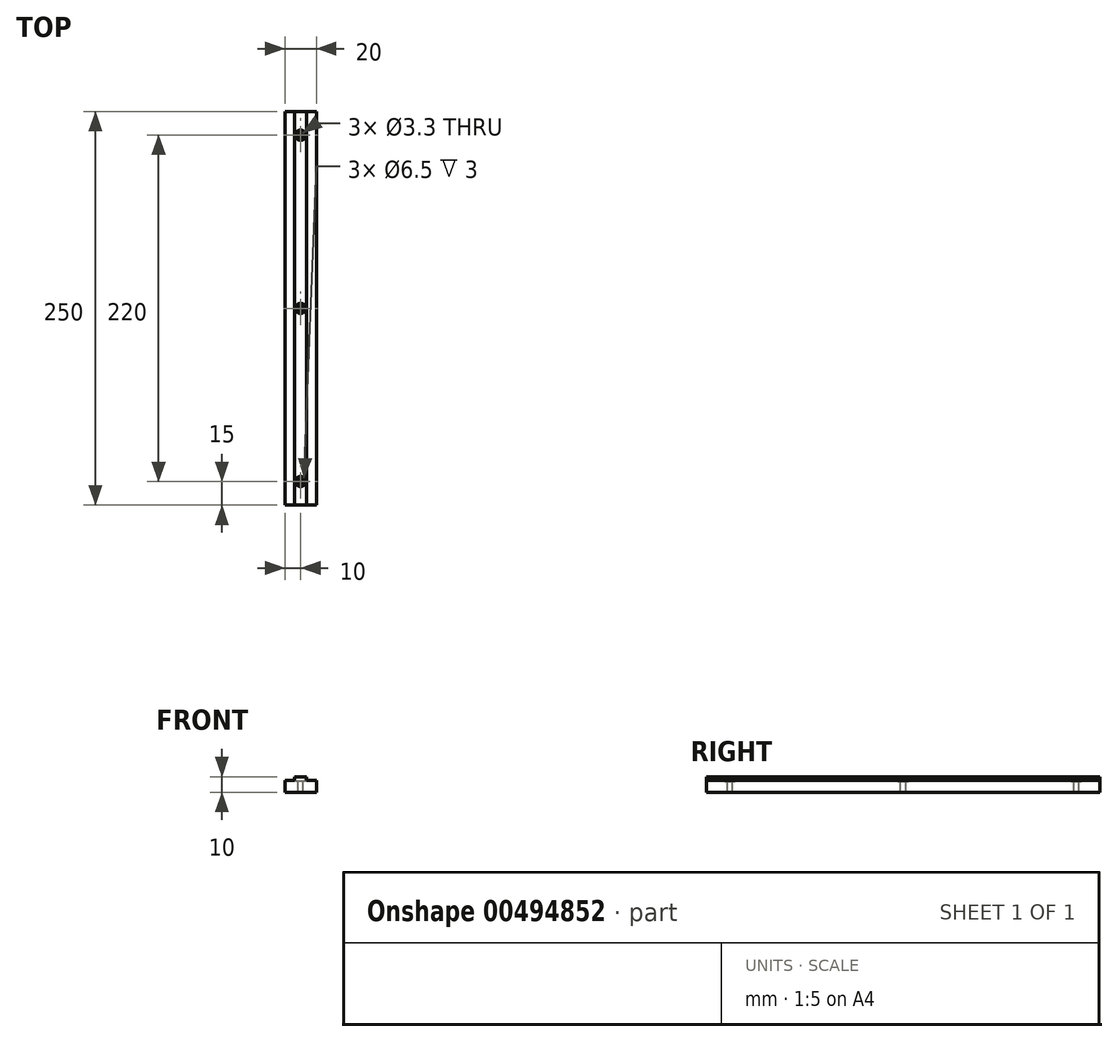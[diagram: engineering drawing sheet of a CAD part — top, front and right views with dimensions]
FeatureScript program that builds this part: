
annotation { "Feature Type Name" : "Feature", "Feature Type Description" : "" }
export const myFeature = defineFeature(function(context is Context, id is Id, definition is map)
    precondition{}
    {
        {
            var Q0;
            Q0=qCreatedBy(makeId("Front.planeOp"),FACE);
            var sketch = newSketch(context, id + "F0", { "sketchPlane" : qUnion([Q0])});
            skLineSegment(sketch, "E0.bottom", {"start": v(-10, 0) * mm, "end": v(10, 0) * mm});
            skLineSegment(sketch, "E0.top", {"start": v(-10, 7.7) * mm, "end": v(-3.8, 7.7) * mm});
            skLineSegment(sketch, "E0.left", {"start": v(-10, 0) * mm, "end": v(-10, 7.7) * mm});
            skLineSegment(sketch, "E0.right", {"start": v(10, 0) * mm, "end": v(10, 7.7) * mm});
            skLineSegment(sketch, "E1.top", {"start": v(-3.8, 10) * mm, "end": v(3.8, 10) * mm});
            skLineSegment(sketch, "E1.left", {"start": v(-3.8, 7.7) * mm, "end": v(-3.8, 10) * mm});
            skLineSegment(sketch, "E1.right", {"start": v(3.8, 7.7) * mm, "end": v(3.8, 10) * mm});
            skLineSegment(sketch, "E2.trimOffspring", {"start": v(3.8, 7.7) * mm, "end": v(10, 7.7) * mm});
            skSolve(sketch);
        }
        {
            var Q0;
            Q0=qSketchRegion(id+"F0",true);
            extrude(context, id + "F1", {"entities" : qUnion([Q0]), "oppositeDirection" : true, "depth" : 250 * mm});
        }
        {
            var Q0;
            Q0=makeQuery(id+"F1.opExtrude","SWEPT_FACE",FACE,{"disambiguationData":[OSD([sQuery(id+"F0.wireOp",EDGE,"E1.top")])]});
            var sketch = newSketch(context, id + "F2", { "sketchPlane" : qUnion([Q0])});
            skPoint(sketch, "E3", {"position": v(0, 15) * mm});
            skPoint(sketch, "E4", {"position": v(0, 125) * mm});
            skPoint(sketch, "E5", {"position": v(0, 235) * mm});
            skSolve(sketch);
        }
        {
            var Q0;
            Q0=sQuery(id+"F2.wireOp",VERTEX,"E3");
            var Q1;
            Q1=sQuery(id+"F2.wireOp",VERTEX,"E4");
            var Q2;
            Q2=sQuery(id+"F2.wireOp",VERTEX,"E5");
            var Q3;
            Q3=makeQuery(id+"F1.opExtrude","SWEPT_BODY",BODY,{"disambiguationData":[OSD([sQuery(id+"F0.wireOp",EDGE,"E0.bottom"),sQuery(id+"F0.wireOp",EDGE,"E0.top"),sQuery(id+"F0.wireOp",EDGE,"E0.left"),sQuery(id+"F0.wireOp",EDGE,"E0.right"),sQuery(id+"F0.wireOp",EDGE,"E1.top"),sQuery(id+"F0.wireOp",EDGE,"E1.left"),sQuery(id+"F0.wireOp",EDGE,"E1.right"),sQuery(id+"F0.wireOp",EDGE,"E2.trimOffspring")])]});
            hole(context, id + "F3", {"style" : HoleStyle.C_BORE, "endStyle" : HoleEndStyle.THROUGH, "standardTappedOrClearance" : lookupTablePath({ "standard" : "ISO", "fit" : "Normal", "size" : "M3", "type" : "Clearance" }), "standardBlindInLast" : lookupTablePath({ "fit" : "Standard", "standard" : "ISO", "size" : "M3", "type" : "Clearance" }), "holeDiameter" : 3.3 * mm, "cBoreDiameter" : 6.5 * mm, "cBoreDepth" : 3 * mm, "isTappedThrough" : true, "tappedDepth" : 7.6 * mm, "tapClearance" : 3, "locations" : qUnion([Q0, Q1, Q2]), "scope" : qUnion([Q3])});
        }
    });
